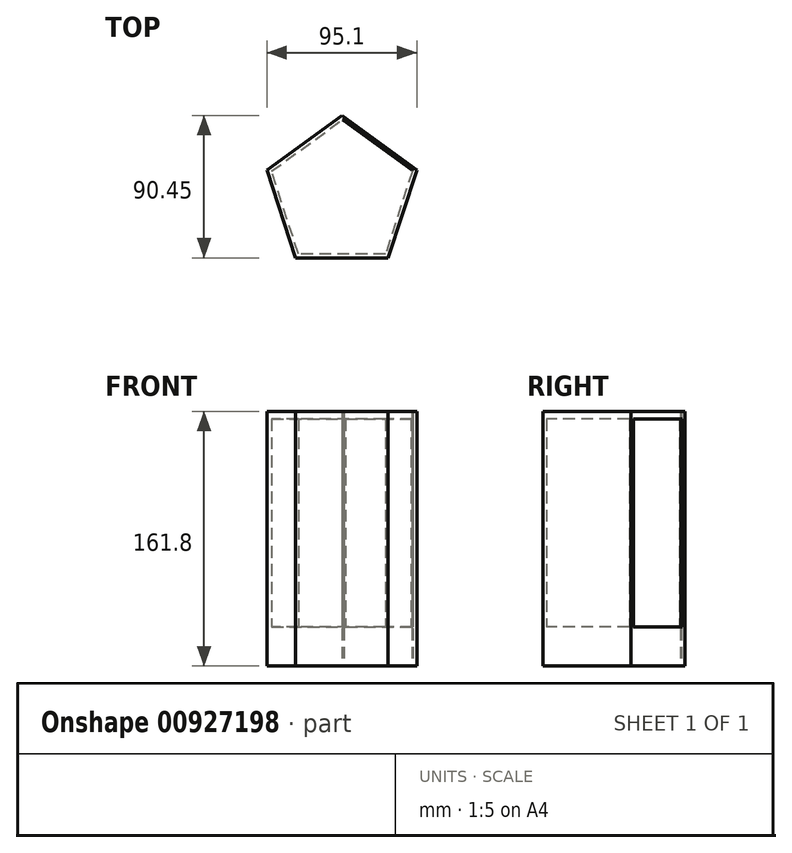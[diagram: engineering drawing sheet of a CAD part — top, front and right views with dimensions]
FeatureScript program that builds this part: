
annotation { "Feature Type Name" : "Feature", "Feature Type Description" : "" }
export const myFeature = defineFeature(function(context is Context, id is Id, definition is map)
    precondition{}
    {
        {
            assignVariable(context, id + "F0", {"name" : "goldenratio", "anyValue" : 1.62});
        }
        {
            assignVariable(context, id + "F1", {"name" : "width", "anyValue" : 100});
        }
        {
            assignVariable(context, id + "F2", {"name" : "height", "anyValue" : getVariable(context, 'width') * getVariable(context, 'goldenratio')});
        }
        {
            var Q0;
            Q0=qCreatedBy(makeId("Top.planeOp"),FACE);
            var sketch = newSketch(context, id + "F3", { "sketchPlane" : qUnion([Q0])});
            skCircle(sketch, "E0.cCircle", {"center": v(0, 0) * mm, "radius": 50 * mm, "construction": true});
            skLineSegment(sketch, "E0.0", {"start": v(0, 50) * mm, "end": v(2.4, 48.26) * mm});
            skLineSegment(sketch, "E0.1", {"start": v(47.55, 15.45) * mm, "end": v(29.39, -40.45) * mm});
            skLineSegment(sketch, "E0.2", {"start": v(29.39, -40.45) * mm, "end": v(-29.39, -40.45) * mm});
            skLineSegment(sketch, "E0.3", {"start": v(-29.39, -40.45) * mm, "end": v(-47.55, 15.45) * mm});
            skLineSegment(sketch, "E0.4", {"start": v(-47.55, 15.45) * mm, "end": v(0, 50) * mm});
            skCircle(sketch, "E1.cCircle", {"center": v(0, 0) * mm, "radius": 47 * mm, "construction": true});
            skLineSegment(sketch, "E1.0", {"start": v(0, 47) * mm, "end": v(0.97, 46.3) * mm});
            skLineSegment(sketch, "E1.1", {"start": v(44.7, 14.52) * mm, "end": v(27.63, -38.02) * mm});
            skLineSegment(sketch, "E1.2", {"start": v(27.63, -38.02) * mm, "end": v(-27.63, -38.02) * mm});
            skLineSegment(sketch, "E1.3", {"start": v(-27.63, -38.02) * mm, "end": v(-44.7, 14.52) * mm});
            skLineSegment(sketch, "E1.4", {"start": v(-44.7, 14.52) * mm, "end": v(0, 47) * mm});
            skLineSegment(sketch, "E2", {"start": v(0.97, 46.3) * mm, "end": v(44.7, 14.52) * mm});
            skLineSegment(sketch, "E3", {"start": v(2.4, 48.26) * mm, "end": v(47.55, 15.45) * mm});
            skLineSegment(sketch, "E4", {"start": v(1.32, 47.8) * mm, "end": v(1.8, 47.45) * mm});
            skLineSegment(sketch, "E5", {"start": v(1.8, 47.45) * mm, "end": v(2.4, 48.26) * mm});
            skLineSegment(sketch, "E6", {"start": v(0.74, 47) * mm, "end": v(1.32, 47.8) * mm});
            skLineSegment(sketch, "E7", {"start": v(0.74, 47) * mm, "end": v(1.22, 46.64) * mm});
            skLineSegment(sketch, "E8", {"start": v(1.22, 46.64) * mm, "end": v(0.97, 46.3) * mm});
            skLineSegment(sketch, "E9", {"start": v(0, 0) * mm, "end": v(35.92, 49.44) * mm, "construction": true});
            skLineSegment(sketch, "E10.MirrorCS", {"start": v(44.57, 16.38) * mm, "end": v(45.16, 17.2) * mm});
            skLineSegment(sketch, "E11.MirrorCS", {"start": v(45.05, 16.03) * mm, "end": v(44.57, 16.38) * mm});
            skLineSegment(sketch, "E12.MirrorCS", {"start": v(44.47, 15.22) * mm, "end": v(45.05, 16.03) * mm});
            skLineSegment(sketch, "E13.MirrorCS", {"start": v(44.47, 15.22) * mm, "end": v(43.98, 15.57) * mm});
            skLineSegment(sketch, "E14.MirrorCS", {"start": v(43.98, 15.57) * mm, "end": v(43.73, 15.23) * mm});
            skLineSegment(sketch, "E15.MirrorCS", {"start": v(44.7, 14.52) * mm, "end": v(43.73, 15.23) * mm});
            skLineSegment(sketch, "E16", {"start": v(1.32, 47.8) * mm, "end": v(45.05, 16.03) * mm});
            skLineSegment(sketch, "E17", {"start": v(44.47, 15.22) * mm, "end": v(0.74, 47) * mm});
            skSolve(sketch);
        }
        {
            var Q0;
            Q0=makeQuery(id+"F3.imprint","IMPRINT",FACE,{"disambiguationData":[TD([[makeQuery(id+"F3.imprint","IMPRINT",EDGE,{"derivedFrom":sQuery(id+"F3.wireOp",EDGE,"E0.0")}),-1.0]])]});
            extrude(context, id + "F4", {"entities" : qUnion([Q0]), "depth" : (getVariable(context, 'height')) * mm, "offsetDistance" : 25 * mm});
        }
        {
            var Q0;
            Q0 = qSketchRegion(id + "F3", true);
            var Q1;
            Q1=makeQuery(id+"F3.imprint","IMPRINT",FACE,{"disambiguationData":[TD([[makeQuery(id+"F3.imprint","IMPRINT",EDGE,{"derivedFrom":sQuery(id+"F3.wireOp",EDGE,"E1.0")}),-1.0]])]});
            var Q2;
            {var subQ3=sQuery(id+"F3.wireOp",EDGE,"E6");Q2=makeQuery(id+"F3.imprint","IMPRINT",FACE,{"disambiguationData":[TD([[makeQuery(id+"F3.imprint","IMPRINT",EDGE,{"derivedFrom":subQ3}),-1.0]])]});}
            var Q3;
            Q3=makeQuery(id+"F3.imprint","IMPRINT",FACE,{"disambiguationData":[TD([[makeQuery(id+"F3.imprint","IMPRINT",EDGE,{"derivedFrom":sQuery(id+"F3.wireOp",EDGE,"E2")}),1.0]])]});
            extrude(context, id + "F5", {"entities" : qUnion([Q0, Q1, Q2, Q3]), "operationType" : NewBodyOperationType.ADD, "depth" : 25 * mm, "offsetDistance" : 25 * mm});
        }
        {
            var Q0;
            Q0=makeQuery(id+"F5.opExtrude","CAP_FACE",FACE,{"disambiguationData":[OSD([sQuery(id+"F3.wireOp",EDGE,"E0.0"),sQuery(id+"F3.wireOp",EDGE,"E0.1"),sQuery(id+"F3.wireOp",EDGE,"E0.2"),sQuery(id+"F3.wireOp",EDGE,"E0.3"),sQuery(id+"F3.wireOp",EDGE,"E0.4"),sQuery(id+"F3.wireOp",EDGE,"E3")])],"isStart":false});
            var Q1;
            Q1=makeQuery(id+"F4.opExtrude","CAP_FACE",FACE,{"disambiguationData":[OSD([sQuery(id+"F3.wireOp",EDGE,"E0.0"),sQuery(id+"F3.wireOp",EDGE,"E0.1"),sQuery(id+"F3.wireOp",EDGE,"E0.2"),sQuery(id+"F3.wireOp",EDGE,"E0.3"),sQuery(id+"F3.wireOp",EDGE,"E0.4"),sQuery(id+"F3.wireOp",EDGE,"E1.0"),sQuery(id+"F3.wireOp",EDGE,"E1.1"),sQuery(id+"F3.wireOp",EDGE,"E1.2"),sQuery(id+"F3.wireOp",EDGE,"E1.3"),sQuery(id+"F3.wireOp",EDGE,"E1.4"),sQuery(id+"F3.wireOp",EDGE,"E3"),sQuery(id+"F3.wireOp",EDGE,"E5"),sQuery(id+"F3.wireOp",EDGE,"E6"),sQuery(id+"F3.wireOp",EDGE,"E8"),sQuery(id+"F3.wireOp",EDGE,"E10.MirrorCS"),sQuery(id+"F3.wireOp",EDGE,"E12.MirrorCS"),sQuery(id+"F3.wireOp",EDGE,"E14.MirrorCS"),sQuery(id+"F3.wireOp",EDGE,"E15.MirrorCS"),sQuery(id+"F3.wireOp",EDGE,"E16"),sQuery(id+"F3.wireOp",EDGE,"E17")])],"isStart":false});
            var Q2;
            Q2=makeQuery(id+"F4.opExtrude","CAP_FACE",FACE,{"disambiguationData":[OSD([sQuery(id+"F3.wireOp",EDGE,"E0.0"),sQuery(id+"F3.wireOp",EDGE,"E0.1"),sQuery(id+"F3.wireOp",EDGE,"E0.2"),sQuery(id+"F3.wireOp",EDGE,"E0.3"),sQuery(id+"F3.wireOp",EDGE,"E0.4"),sQuery(id+"F3.wireOp",EDGE,"E1.0"),sQuery(id+"F3.wireOp",EDGE,"E1.1"),sQuery(id+"F3.wireOp",EDGE,"E1.2"),sQuery(id+"F3.wireOp",EDGE,"E1.3"),sQuery(id+"F3.wireOp",EDGE,"E1.4"),sQuery(id+"F3.wireOp",EDGE,"E3"),sQuery(id+"F3.wireOp",EDGE,"E5"),sQuery(id+"F3.wireOp",EDGE,"E6"),sQuery(id+"F3.wireOp",EDGE,"E8"),sQuery(id+"F3.wireOp",EDGE,"E10.MirrorCS"),sQuery(id+"F3.wireOp",EDGE,"E12.MirrorCS"),sQuery(id+"F3.wireOp",EDGE,"E14.MirrorCS"),sQuery(id+"F3.wireOp",EDGE,"E15.MirrorCS"),sQuery(id+"F3.wireOp",EDGE,"E16"),sQuery(id+"F3.wireOp",EDGE,"E17")])],"isStart":false});
            extrude(context, id + "F6", {"entities" : qUnion([Q0]), "operationType" : NewBodyOperationType.ADD, "endBound" : BoundingType.UP_TO_SURFACE, "depth" : 25 * mm, "endBoundEntityFace" : qUnion([Q1]), "offsetDistance" : 25 * mm, "offsetOppositeDirection" : true, "hasSecondDirection" : true, "secondDirectionBound" : SecondDirectionBoundingType.UP_TO_SURFACE, "secondDirectionOppositeDirection" : false, "secondDirectionDepth" : 25 * mm, "secondDirectionBoundEntityFace" : qUnion([Q2]), "hasSecondDirectionOffset" : true, "secondDirectionOffsetDistance" : 5 * mm});
        }
        {
            var Q0;
            {var subQ3=sQuery(id+"F3.wireOp",EDGE,"E6");Q0=makeQuery(id+"F3.imprint","IMPRINT",FACE,{"disambiguationData":[TD([[makeQuery(id+"F3.imprint","IMPRINT",EDGE,{"derivedFrom":subQ3}),-1.0]])]});}
            extrude(context, id + "F7", {"entities" : qUnion([Q0]), "depth" : (getVariable(context, 'height')) * mm, "offsetDistance" : 25 * mm});
        }
    });
